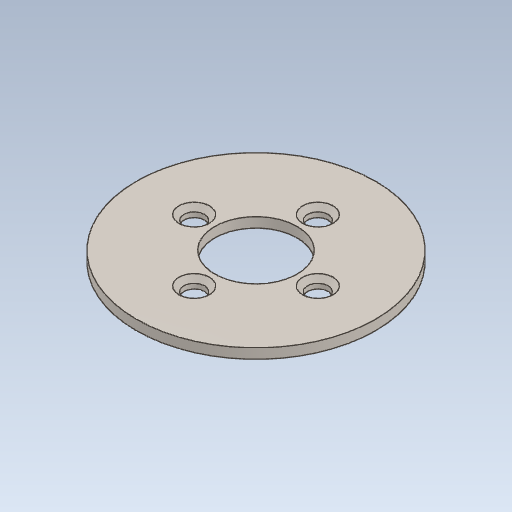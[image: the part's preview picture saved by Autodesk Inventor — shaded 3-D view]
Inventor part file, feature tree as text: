
AUTODESK INVENTOR PART (.ipt)
format: ipt  version: 2020.3 (Build 243373000, 373)  size: 104,448 bytes
history: native  units: in
note: dims shown in document units (in); Inventor stores cm internally (conversion verified against a paired STEP export)
features: chamfer x1
ambient origin geometry x8: Origin, YZ Plane, XZ Plane, XY Plane, X Axis, Y Axis, Z Axis, Center Point
bodies: Solid1 (feature_tree)
feature tree (1):
  chamfer  "Chamfer1"  [1 undecoded]
note: 1 required parameter value undecoded (feature->parameter linkage not recoverable at this tier; creation-order binding heuristic only, values carry confidence <= 0.55)
